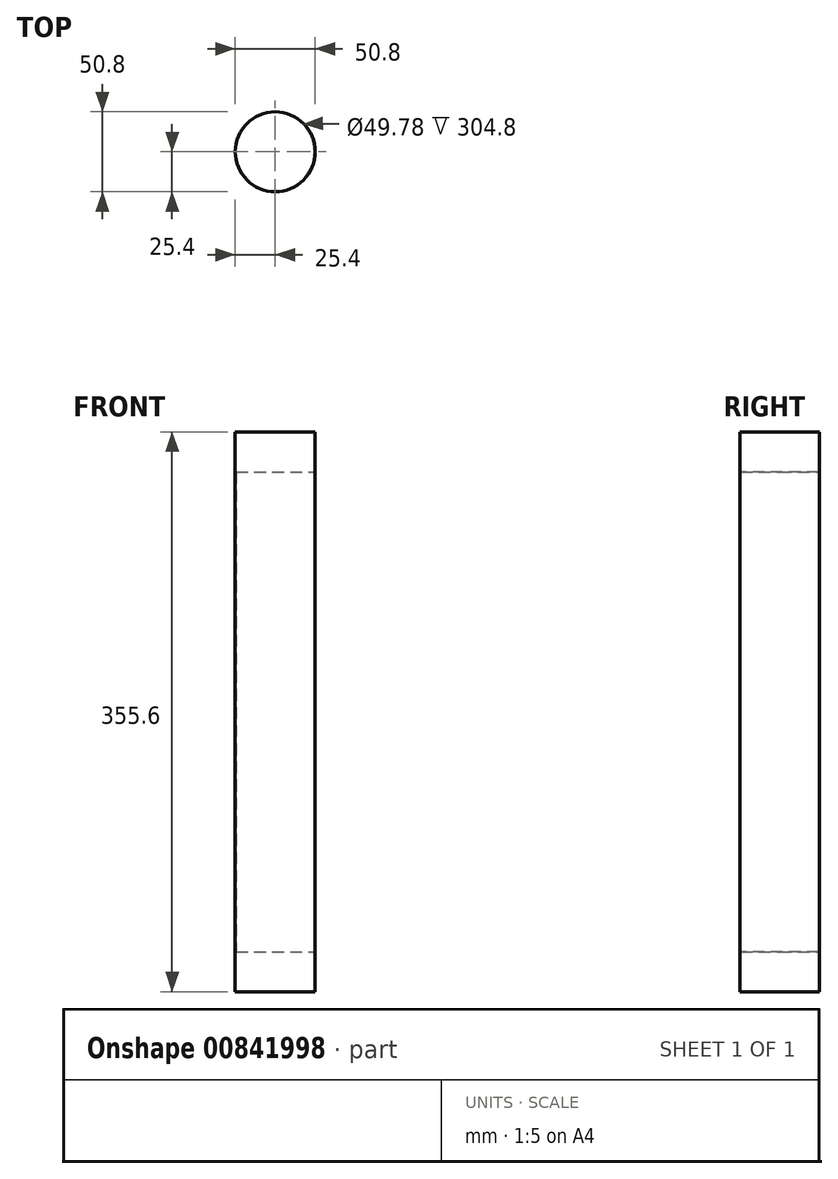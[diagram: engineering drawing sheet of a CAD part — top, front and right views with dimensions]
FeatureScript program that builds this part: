
annotation { "Feature Type Name" : "Feature", "Feature Type Description" : "" }
export const myFeature = defineFeature(function(context is Context, id is Id, definition is map)
    precondition{}
    {
        {
            var Q0;
            Q0=qCreatedBy(makeId("Front.planeOp"),FACE);
            var sketch = newSketch(context, id + "F0", { "sketchPlane" : qUnion([Q0])});
            skLineSegment(sketch, "E0.bottom", {"start": v(-25.4, 177.8) * mm, "end": v(25.4, 177.8) * mm});
            skLineSegment(sketch, "E0.top", {"start": v(-25.4, -177.8) * mm, "end": v(25.4, -177.8) * mm});
            skLineSegment(sketch, "E0.left", {"start": v(-25.4, 177.8) * mm, "end": v(-25.4, -177.8) * mm});
            skLineSegment(sketch, "E0.right", {"start": v(25.4, 177.8) * mm, "end": v(25.4, -177.8) * mm});
            skPoint(sketch, "E0.middle", {"position": v(0, 0) * mm});
            skLineSegment(sketch, "E1.bottom", {"start": v(-24.9, 152.4) * mm, "end": v(24.9, 152.4) * mm});
            skLineSegment(sketch, "E1.top", {"start": v(-24.9, -152.4) * mm, "end": v(24.9, -152.4) * mm});
            skLineSegment(sketch, "E1.left", {"start": v(-24.9, 152.4) * mm, "end": v(-24.9, -152.4) * mm});
            skLineSegment(sketch, "E1.right", {"start": v(24.9, 152.4) * mm, "end": v(24.9, -152.4) * mm});
            skLineSegment(sketch, "E2", {"start": v(0, -177.8) * mm, "end": v(0, 177.8) * mm});
            skSolve(sketch);
        }
        {
            var Q0;
            {var subQ4=sQuery(id+"F0.wireOp",EDGE,"E0.left");Q0=makeQuery(id+"F0.imprint","IMPRINT",FACE,{"disambiguationData":[TD([[makeQuery(id+"F0.imprint","IMPRINT",EDGE,{"derivedFrom":subQ4}),1.0]])]});}
            var Q1;
            Q1=sQuery(id+"F0.wireOp",EDGE,"E2");
            revolve(context, id + "F1", {"surfaceOperationType" : NewSurfaceOperationType.NEW, "entities" : qUnion([Q0]), "axis" : qUnion([Q1]), "revolveType" : RevolveType.FULL});
        }
    });
